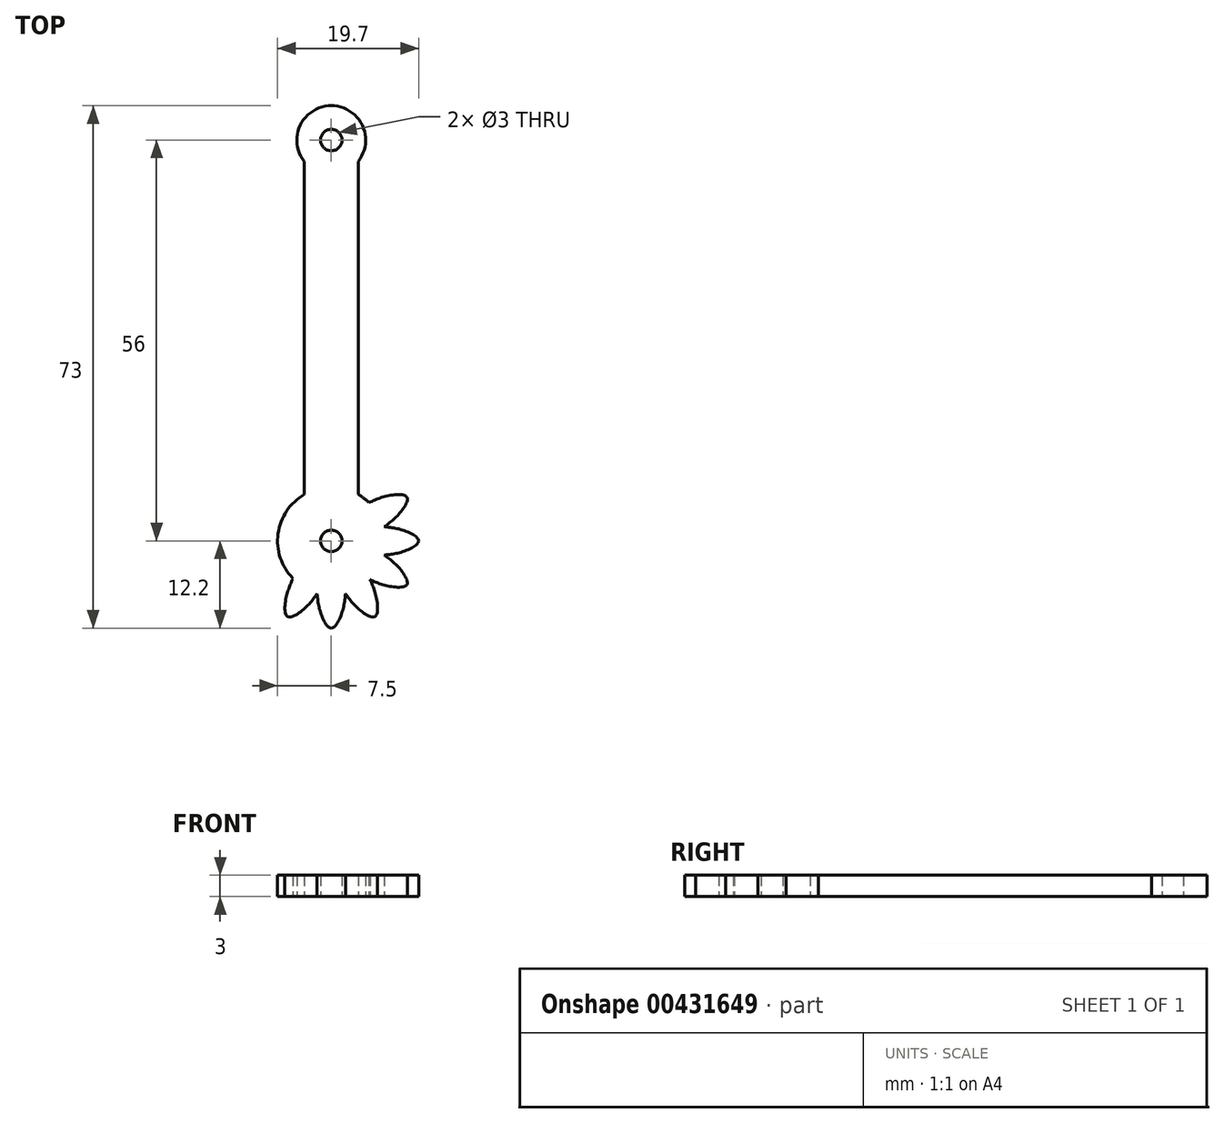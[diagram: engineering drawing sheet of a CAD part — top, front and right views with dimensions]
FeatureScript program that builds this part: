
annotation { "Feature Type Name" : "Feature", "Feature Type Description" : "" }
export const myFeature = defineFeature(function(context is Context, id is Id, definition is map)
    precondition{}
    {
        {
            var Q0;
            Q0=qCreatedBy(makeId("Top.planeOp"),FACE);
            var sketch = newSketch(context, id + "F0", { "sketchPlane" : qUnion([Q0])});
            skLineSegment(sketch, "E0.bottom", {"start": v(0, 0) * mm, "end": v(0, 0) * mm});
            skLineSegment(sketch, "E0.top", {"start": v(0, 50) * mm, "end": v(7.5, 50) * mm, "construction": true});
            skLineSegment(sketch, "E0.left", {"start": v(0, 0) * mm, "end": v(0, 0) * mm});
            skLineSegment(sketch, "E0.right", {"start": v(7.5, 0) * mm, "end": v(7.5, 0) * mm});
            skLineSegment(sketch, "E1", {"start": v(3.75, 50) * mm, "end": v(3.75, 53) * mm, "construction": true});
            skLineSegment(sketch, "E2", {"start": v(3.75, 0) * mm, "end": v(3.75, -3) * mm, "construction": true});
            skCircle(sketch, "E3", {"center": v(3.75, -3) * mm, "radius": 1.5 * mm});
            skCircle(sketch, "E4", {"center": v(3.75, 53) * mm, "radius": 1.5 * mm});
            skArc(sketch, "E5", {"start": v(0, 50) * mm, "mid": v(3.75, 48.2) * mm, "end": v(7.5, 50) * mm, "construction": true});
            skArc(sketch, "E6", {"start": v(7.5, 50) * mm, "mid": v(3.75, 57.8) * mm, "end": v(0, 50) * mm});
            skLineSegment(sketch, "E7", {"start": v(0, 0) * mm, "end": v(0, 50) * mm});
            skLineSegment(sketch, "E8", {"start": v(0, 0) * mm, "end": v(7.5, 0) * mm, "construction": true});
            skLineSegment(sketch, "E9", {"start": v(7.5, 0) * mm, "end": v(7.5, 50) * mm});
            skCircle(sketch, "E10", {"center": v(3.75, -3) * mm, "radius": 7.5 * mm});
            skLineSegment(sketch, "E11", {"start": v(3.75, -3) * mm, "end": v(15.95, -3) * mm});
            skLineSegment(sketch, "E12", {"start": v(11.25, -3) * mm, "end": v(11.25, -5) * mm});
            skLineSegment(sketch, "E13", {"start": v(11.25, -5) * mm, "end": v(11.25, -1) * mm, "construction": true});
            skLineSegment(sketch, "E14", {"start": v(11.25, -1) * mm, "end": v(10.98, -1) * mm});
            skLineSegment(sketch, "E15", {"start": v(11.25, -5) * mm, "end": v(10.98, -5) * mm});
            skLineSegment(sketch, "E16", {"start": v(11.25, -3) * mm, "end": v(13.75, -3) * mm, "construction": true});
            skLineSegment(sketch, "E17", {"start": v(13.75, -3) * mm, "end": v(13.75, -1.5) * mm, "construction": true});
            skLineSegment(sketch, "E18", {"start": v(13.75, -1.5) * mm, "end": v(13.75, -4.5) * mm, "construction": true});
            skPoint(sketch, "E18.endSnap0", {"position": v(13.75, -2.25) * mm});
            skFitSpline(sketch, "E19", {"points": [v(10.98, -1) * mm, v(13.75, -1.5) * mm, v(15.95, -3) * mm, v(13.75, -4.5) * mm, v(10.98, -5) * mm], "startDerivative": vector(10.14, -1.04) * mm, "endDerivative": vector(-10.14, -1.04) * mm});
            skSolve(sketch);
        }
        {
            var Q0;
            Q0=makeQuery(id+"F0.imprint","IMPRINT",FACE,{"disambiguationData":[TD([[makeQuery(id+"F0.imprint","IMPRINT",EDGE,{"derivedFrom":sQuery(id+"F0.wireOp",EDGE,"E3")}),-1.0]])]});
            var Q1;
            {var subQ0=sQuery(id+"F0.wireOp",EDGE,"E11");var subQ3=sQuery(id+"F0.wireOp",EDGE,"E19");var subQ5=makeQuery(id+"F0.imprint","INTERSECT",VERTEX,{"derivedFrom":[subQ0,subQ3]});Q1=makeQuery(id+"F0.imprint","IMPRINT",FACE,{"disambiguationData":[TD([[makeQuery(id+"F0.imprint","IMPRINT",EDGE,{"disambiguationData":[TD([[subQ5,1.0]])],"derivedFrom":subQ3}),-1.0]])]});}
            var Q2;
            {var subQ0=sQuery(id+"F0.wireOp",EDGE,"E19");var subQ1=sQuery(id+"F0.wireOp",EDGE,"E11");var subQ2=makeQuery(id+"F0.imprint","INTERSECT",VERTEX,{"derivedFrom":[subQ1,subQ0]});Q2=makeQuery(id+"F0.imprint","IMPRINT",FACE,{"disambiguationData":[TD([[makeQuery(id+"F0.imprint","IMPRINT",EDGE,{"disambiguationData":[TD([[subQ2,-1.0]])],"derivedFrom":subQ0}),-1.0]])]});}
            var Q3;
            {var subQ0=sQuery(id+"F0.wireOp",EDGE,"E12");var subQ3=sQuery(id+"F0.wireOp",EDGE,"E19");var subQ5=makeQuery(id+"F0.imprint","INTERSECT",VERTEX,{"derivedFrom":[subQ0,subQ3]});Q3=makeQuery(id+"F0.imprint","IMPRINT",FACE,{"disambiguationData":[TD([[makeQuery(id+"F0.imprint","IMPRINT",EDGE,{"disambiguationData":[TD([[subQ5,1.0]])],"derivedFrom":subQ0}),-1.0]])]});}
            extrude(context, id + "F1", {"entities" : qUnion([Q0, Q1, Q2, Q3]), "depth" : 3 * mm});
        }
        {
            var Q0;
            Q0=makeQuery(id+"F1.opExtrude","SWEPT_BODY",BODY,{"disambiguationData":[OSD([sQuery(id+"F0.wireOp",EDGE,"E3"),sQuery(id+"F0.wireOp",EDGE,"E10"),sQuery(id+"F0.wireOp",EDGE,"E19")])]});
            var Q1;
            Q1=makeQuery(id+"F1.opExtrude","CAP_EDGE",EDGE,{"disambiguationData":[OSD([sQuery(id+"F0.wireOp",EDGE,"E3")])],"isStart":false});
            circularPattern(context, id + "F2", {"entities" : qUnion([Q0]), "axis" : qUnion([Q1]), "angle" : 120 * degree, "instanceCount" : 5, "oppositeDirection" : true, "equalSpace" : true});
        }
        {
            var Q0;
            Q0=makeQuery(id+"F1.opExtrude","SWEPT_BODY",BODY,{"disambiguationData":[OSD([sQuery(id+"F0.wireOp",EDGE,"E3"),sQuery(id+"F0.wireOp",EDGE,"E10"),sQuery(id+"F0.wireOp",EDGE,"E19")])]});
            var Q1;
            Q1=sQuery(id+"F0.wireOp",EDGE,"E3");
            circularPattern(context, id + "F3", {"entities" : qUnion([Q0]), "axis" : qUnion([Q1]), "angle" : 30 * degree, "instanceCount" : 2, "equalSpace" : true});
        }
        {
            var Q0;
            Q0=makeQuery(id+"F0.imprint","IMPRINT",FACE,{"disambiguationData":[TD([[makeQuery(id+"F0.imprint","IMPRINT",EDGE,{"derivedFrom":sQuery(id+"F0.wireOp",EDGE,"E4")}),-1.0]])]});
            extrude(context, id + "F4", {"entities" : qUnion([Q0]), "operationType" : NewBodyOperationType.ADD, "depth" : 3 * mm});
        }
    });
